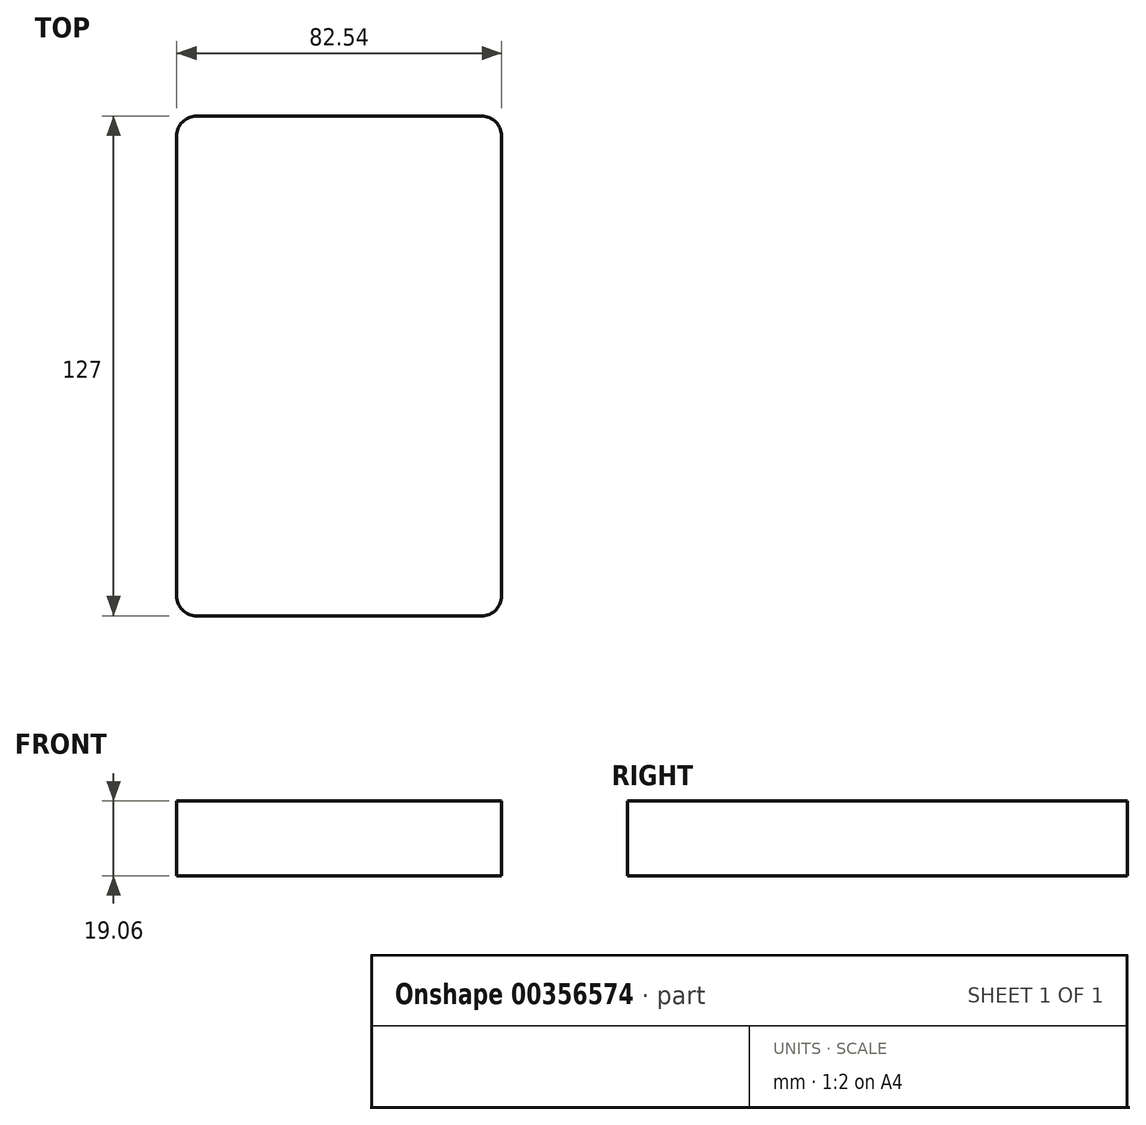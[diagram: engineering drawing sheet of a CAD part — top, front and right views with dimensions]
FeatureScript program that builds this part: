
annotation { "Feature Type Name" : "Feature", "Feature Type Description" : "" }
export const myFeature = defineFeature(function(context is Context, id is Id, definition is map)
    precondition{}
    {
        {
            var Q0;
            Q0=qCreatedBy(makeId("Front.planeOp"),FACE);
            var sketch = newSketch(context, id + "F0", { "sketchPlane" : qUnion([Q0])});
            skLineSegment(sketch, "E0.rect.bottom", {"start": v(-41.28, 9.52) * mm, "end": v(41.28, 9.52) * mm});
            skLineSegment(sketch, "E0.rect.top", {"start": v(-41.28, -9.52) * mm, "end": v(41.28, -9.52) * mm});
            skLineSegment(sketch, "E0.rect.left", {"start": v(-41.28, 9.52) * mm, "end": v(-41.28, -9.52) * mm});
            skLineSegment(sketch, "E0.rect.right", {"start": v(41.28, 9.52) * mm, "end": v(41.28, -9.52) * mm});
            skPoint(sketch, "E0.rect.middle", {"position": v(0, 0) * mm});
            skLineSegment(sketch, "E1", {"start": v(41.28, 9.52) * mm, "end": v(41.28, 27) * mm});
            skArc(sketch, "E2", {"start": v(41.28, 27) * mm, "mid": v(45.92, 38.23) * mm, "end": v(57.15, 42.88) * mm});
            skLineSegment(sketch, "E3", {"start": v(57.15, 42.88) * mm, "end": v(85.72, 42.88) * mm});
            skLineSegment(sketch, "E4.rect.bottom", {"start": v(60.32, 38.1) * mm, "end": v(111.12, 38.1) * mm});
            skLineSegment(sketch, "E4.rect.top", {"start": v(60.32, 66.68) * mm, "end": v(111.12, 66.68) * mm});
            skLineSegment(sketch, "E4.rect.left", {"start": v(60.32, 38.1) * mm, "end": v(60.32, 66.68) * mm});
            skLineSegment(sketch, "E4.rect.right", {"start": v(111.13, 38.1) * mm, "end": v(111.12, 66.68) * mm});
            skPoint(sketch, "E4.rect.middle", {"position": v(85.72, 52.39) * mm});
            skLineSegment(sketch, "E5.0", {"start": v(57.15, 61.93) * mm, "end": v(85.72, 61.93) * mm});
            skArc(sketch, "E5.1", {"start": v(22.23, 27) * mm, "mid": v(32.45, 51.7) * mm, "end": v(57.15, 61.93) * mm});
            skLineSegment(sketch, "E5.2", {"start": v(22.23, 9.52) * mm, "end": v(22.23, 27) * mm});
            skLineSegment(sketch, "E6", {"start": v(85.72, 38.1) * mm, "end": v(85.72, 66.68) * mm});
            skFitSpline(sketch, "E7", {"points": [v(-41.28, 9.53) * mm, v(57.15, 61.93) * mm], "startDerivative": vector(5.2, 92.34) * mm, "endDerivative": vector(120.92, 4.22) * mm});
            skSolve(sketch);
        }
        {
            var Q0;
            Q0=makeQuery(id+"F0.imprint","IMPRINT",FACE,{"disambiguationData":[TD([[makeQuery(id+"F0.imprint","IMPRINT",EDGE,{"derivedFrom":sQuery(id+"F0.wireOp",EDGE,"E0.rect.top")}),1.0]])]});
            extrude(context, id + "F1", {"entities" : qUnion([Q0]), "endBound" : BoundingType.SYMMETRIC, "depth" : 127 * mm});
        }
        {
            var Q0;
            Q0=makeQuery(id+"F1.opExtrude","CAP_EDGE",EDGE,{"disambiguationData":[OSD([sQuery(id+"F0.wireOp",EDGE,"E0.rect.right")])],"isStart":false});
            var Q1;
            Q1=makeQuery(id+"F1.opExtrude","CAP_EDGE",EDGE,{"disambiguationData":[OSD([sQuery(id+"F0.wireOp",EDGE,"E0.rect.left")])],"isStart":false});
            var Q2;
            Q2=makeQuery(id+"F1.opExtrude","CAP_EDGE",EDGE,{"disambiguationData":[OSD([sQuery(id+"F0.wireOp",EDGE,"E0.rect.right")])],"isStart":true});
            var Q3;
            Q3=makeQuery(id+"F1.opExtrude","CAP_EDGE",EDGE,{"disambiguationData":[OSD([sQuery(id+"F0.wireOp",EDGE,"E0.rect.left")])],"isStart":true});
            fillet(context, id + "F2", {"entities" : qUnion([Q0, Q1, Q2, Q3]), "radius" : 5.08 * mm, "tangentPropagation" : true, "allowEdgeOverflow" : false});
        }
    });
